# Revit family: Casement_30.5_E_Side_Hung_Standard
name_source: partatom
category: Windows
revit_build: Autodesk Revit 2014 (Build: 20130308_1515(x64)
units: mm (PartAtom-declared; Revit-internal decimal feet)

## types (17) — shared parameters
Aluminium Thickness = 1 mm  [stored 0.00328084 ft]
Area Pane Left Top = 0.52 m²
Bead SG Gap = 13 mm  [stored 0.0426509 ft]
Casement Dimension = 31 mm  [stored 0.101706 ft]
Custom Sash Height = 1154 mm  [stored 3.78609 ft]
Custom Sash Width = 554 mm  [stored 1.81759 ft]
DG Extrusion Start = 5 mm  [stored 0.0164042 ft]
DG Gasket Finish = Double Glazing Gasket Material
DG Thickness = 3 mm  [stored 0.00984252 ft]
Default Sill Height = 800 mm  [stored 2.62467 ft]
Depth Bead = 17 mm
Description = Window 30.5mm, Type E side hung
Double Glazing = No
Frame Center Offset = 15 mm  [stored 0.0492126 ft]
Height Panel 1 = 1139 mm  [stored 3.73688 ft]
Height Sash = 1124 mm  [stored 3.68766 ft]
Height Sash Opening = 1154 mm  [stored 3.78609 ft]
Length Transom = 540 mm  [stored 1.77165 ft]
Limit Fixed Pane Height Max = 1800 mm
Limit Fixed Pane Height Min = 200 mm  [stored 0.656168 ft]
Limit Fixed Pane Width Max = 1500 mm
Limit Fixed Pane Width Min = 200 mm  [stored 0.656168 ft]
Limit Sash Height Max = 1200 mm
Limit Sash Height Min = 300 mm  [stored 0.984252 ft]
Limit Sash Width Max = 600 mm  [stored 1.9685 ft]
Limit Sash Width Min = 300 mm  [stored 0.984252 ft]
Limit Window Height Max = 1860 mm
Limit Window Height Min = 1430 mm  [stored 4.6916 ft]
Limit Window Width Max = 2130 mm
Limit Window Width Min = 830 mm  [stored 2.7231 ft]
Manufacturer = Crealco
Max System DG One Piece Thickness = 3 mm  [stored 0.00984252 ft]
Max System DG Unit Thickness = 18 mm  [stored 0.0590551 ft]
Model = Casement 30.5
Offset Bead SG Center Reversed = 15 mm  [stored 0.0492126 ft]
Offset Mullion Left = 570 mm  [stored 1.87008 ft]
Offset Panel 3 Bead Top = 1200 mm
Offset Panel 4 Left = 600 mm  [stored 1.9685 ft]
Offset Sash Left = 23 mm  [stored 0.0754593 ft]
Offset Sash Top = 23 mm  [stored 0.0754593 ft]
Offset Transom Top = 1170 mm
Offset Window Exterior = 15 mm  [stored 0.0492126 ft]
SG Gasket Thickness = 6 mm  [stored 0.019685 ft]
Sash Center Offset = 12 mm  [stored 0.0393701 ft]
Sash Overlap = 7 mm  [stored 0.0229659 ft]
Sash Spacing Inner = 8 mm  [stored 0.0262467 ft]
URL = http://www.crealco.co.za
Wall Closure = By host
Width Bead = 15 mm  [stored 0.0492126 ft]
Width Fixed Pane Bottom LHS = 540 mm  [stored 1.77165 ft]
Width Panel 1 = 540 mm  [stored 1.77165 ft]
Width Profile = 30 mm  [stored 0.0984252 ft]
Width Sash = 524 mm  [stored 1.71916 ft]
Width Sash Opening = 554 mm  [stored 1.81759 ft]
zero-valued in all types: Window Exterior Offset

## per-type parameters (varying)
| type | Area Pane Left Bottom | Area Pane Right | Clearvue SHGC Value | Clearvue U Value | Custom Windload | Custom Window Height | Custom Window Width | DG Thickness Calc | Depth Mullion | Energy Advantage SHGC Value | Energy Advantage U Value | Height | Height Fixed Pane Bottom LHS | Height Fixed Pane RHS | Intruderprufe LowE SHGC Value | Intruderprufe LowE U Value | Intruderprufe SHGC Value | Intruderprufe U Value | Length Mullion | Max Pane Area | Mullion Depth Windload Based | Width | Width Fixed Pane RHS | Windload Design |
| 305-0915S-1000Pa | 0.13 m² | 0.36 m² | 0.627 | 6.69 | 1000 mm  [stored 3.28084 ft] | 1490 mm  [stored 4.88845 ft] | 890 mm  [stored 2.91995 ft] | 3 mm  [stored 0.00984252 ft] | 54 mm  [stored 0.177165 ft] | 0.563 | 5.23 | 1490 mm  [stored 4.88845 ft] | 260 mm  [stored 0.853018 ft] | 1430 mm  [stored 4.6916 ft] | 0.532 | 5.11 | 0.598 | 6.53 | 1490 mm  [stored 4.88845 ft] | 0.52 m² | 54 mm  [stored 0.177165 ft] | 890 mm  [stored 2.91995 ft] | 260 mm  [stored 0.853018 ft] | 1000 mm  [stored 3.28084 ft] |
| 305-1215S-1000Pa | 0.13 m² | 0.78 m² | 0.71 | 6.85 | 1000 mm  [stored 3.28084 ft] | 1490 mm  [stored 4.88845 ft] | 1190 mm  [stored 3.9042 ft] | 3 mm  [stored 0.00984252 ft] | 54 mm  [stored 0.177165 ft] | 0.635 | 5.15 | 1490 mm  [stored 4.88845 ft] | 260 mm  [stored 0.853018 ft] | 1430 mm  [stored 4.6916 ft] | 0.599 | 5.04 | 0.675 | 6.69 | 1490 mm  [stored 4.88845 ft] | 0.78 m² | 54 mm  [stored 0.177165 ft] | 1190 mm  [stored 3.9042 ft] | 560 mm | 1000 mm  [stored 3.28084 ft] |
| 305-1215S-2000Pa | 0.13 m² | 0.78 m² | 0.711 | 6.19 | 2000 mm | 1490 mm  [stored 4.88845 ft] | 1190 mm  [stored 3.9042 ft] | 3 mm  [stored 0.00984252 ft] | 70 mm  [stored 0.229659 ft] | 0.637 | 5.24 | 1490 mm  [stored 4.88845 ft] | 260 mm  [stored 0.853018 ft] | 1430 mm  [stored 4.6916 ft] | 0.6 | 5.12 | 0.677 | 6.76 | 1490 mm  [stored 4.88845 ft] | 0.78 m² | 70 mm  [stored 0.229659 ft] | 1190 mm  [stored 3.9042 ft] | 560 mm | 2000 mm |
| 305-1515S-1000Pa | 0.13 m² | 1.21 m² | 0.762 | 6.69 | 1000 mm  [stored 3.28084 ft] | 1490 mm  [stored 4.88845 ft] | 1490 mm  [stored 4.88845 ft] | 4 mm  [stored 0.0131234 ft] | 54 mm  [stored 0.177165 ft] | 0.682 | 5.11 | 1490 mm  [stored 4.88845 ft] | 260 mm  [stored 0.853018 ft] | 1430 mm  [stored 4.6916 ft] | 0.641 | 4.99 | 0.725 | 6.79 | 1490 mm  [stored 4.88845 ft] | 1.21 m² | 54 mm  [stored 0.177165 ft] | 1490 mm  [stored 4.88845 ft] | 860 mm  [stored 2.82152 ft] | 1000 mm  [stored 3.28084 ft] |
| 305-1515S-2000Pa | 0.13 m² | 1.21 m² | 0.763 | 7 | 2000 mm | 1490 mm  [stored 4.88845 ft] | 1490 mm  [stored 4.88845 ft] | 4 mm  [stored 0.0131234 ft] | 70 mm  [stored 0.229659 ft] | 0.683 | 5.17 | 1490 mm  [stored 4.88845 ft] | 260 mm  [stored 0.853018 ft] | 1430 mm  [stored 4.6916 ft] | 0.642 | 5.06 | 0.726 | 6.85 | 1490 mm  [stored 4.88845 ft] | 1.21 m² | 70 mm  [stored 0.229659 ft] | 1490 mm  [stored 4.88845 ft] | 860 mm  [stored 2.82152 ft] | 2000 mm |
| 305-0918S-1000Pa | 0.29 m² | 0.43 m² | 0.675 | 7 | 1000 mm  [stored 3.28084 ft] | 1790 mm | 890 mm  [stored 2.91995 ft] | 3 mm  [stored 0.00984252 ft] | 54 mm  [stored 0.177165 ft] | 0.605 | 5.45 | 1790 mm | 560 mm | 1730 mm | 0.572 | 5.29 | 0.644 | 6.84 | 1790 mm | 0.52 m² | 54 mm  [stored 0.177165 ft] | 890 mm  [stored 2.91995 ft] | 260 mm  [stored 0.853018 ft] | 1000 mm  [stored 3.28084 ft] |
| 305-0918S-1500Pa | 0.29 m² | 0.43 m² | 0.677 | 7.08 | 1500 mm | 1790 mm | 890 mm  [stored 2.91995 ft] | 3 mm  [stored 0.00984252 ft] | 70 mm  [stored 0.229659 ft] | 0.607 | 5.52 | 1790 mm | 560 mm | 1730 mm | 0.575 | 5.4 | 0.646 | 6.92 | 1790 mm | 0.52 m² | 70 mm  [stored 0.229659 ft] | 890 mm  [stored 2.91995 ft] | 260 mm  [stored 0.853018 ft] | 1500 mm |
| 305-1218S-1000Pa | 0.29 m² | 0.95 m² | 0.783 | 7.38 | 1000 mm  [stored 3.28084 ft] | 1790 mm | 1190 mm  [stored 3.9042 ft] | 3 mm  [stored 0.00984252 ft] | 54 mm  [stored 0.177165 ft] | 0.701 | 5.5 | 1790 mm | 560 mm | 1730 mm | 0.66 | 5.37 | 0.745 | 7.21 | 1790 mm | 0.95 m² | 54 mm  [stored 0.177165 ft] | 1190 mm  [stored 3.9042 ft] | 560 mm | 1000 mm  [stored 3.28084 ft] |
| 305-1218S-1500Pa | 0.29 m² | 0.95 m² | 0.784 | 7.45 | 1500 mm | 1790 mm | 1190 mm  [stored 3.9042 ft] | 3 mm  [stored 0.00984252 ft] | 70 mm  [stored 0.229659 ft] | 0.702 | 5.58 | 1790 mm | 560 mm | 1730 mm | 0.662 | 5.46 | 0.747 | 7.28 | 1790 mm | 0.95 m² | 70 mm  [stored 0.229659 ft] | 1190 mm  [stored 3.9042 ft] | 560 mm | 1500 mm |
| 305-1518S-1000Pa | 0.29 m² | 1.46 m² | 0 | 7.9 | 1000 mm  [stored 3.28084 ft] | 1790 mm | 1490 mm  [stored 4.88845 ft] | 4 mm  [stored 0.0131234 ft] | 70 mm  [stored 0.229659 ft] | 0 | 7.9 | 1790 mm | 560 mm | 1730 mm | 0.719 | 5.5 | 0.814 | 7.51 | 1790 mm | 1.46 m² | 70 mm  [stored 0.229659 ft] | 1490 mm  [stored 4.88845 ft] | 860 mm  [stored 2.82152 ft] | 1000 mm  [stored 3.28084 ft] |
| 305-0915S-1500Pa | 0.13 m² | 0.36 m² | 0.627 | 6.69 | 1500 mm | 1490 mm  [stored 4.88845 ft] | 890 mm  [stored 2.91995 ft] | 3 mm  [stored 0.00984252 ft] | 54 mm  [stored 0.177165 ft] | 0.563 | 5.23 | 1490 mm  [stored 4.88845 ft] | 260 mm  [stored 0.853018 ft] | 1430 mm  [stored 4.6916 ft] | 0.532 | 5.11 | 0.598 | 6.53 | 1490 mm  [stored 4.88845 ft] | 0.52 m² | 54 mm  [stored 0.177165 ft] | 890 mm  [stored 2.91995 ft] | 260 mm  [stored 0.853018 ft] | 1500 mm |
| 305-0915S-2000Pa | 0.13 m² | 0.36 m² | 0.627 | 6.69 | 2000 mm | 1490 mm  [stored 4.88845 ft] | 890 mm  [stored 2.91995 ft] | 3 mm  [stored 0.00984252 ft] | 54 mm  [stored 0.177165 ft] | 0.563 | 5.23 | 1490 mm  [stored 4.88845 ft] | 260 mm  [stored 0.853018 ft] | 1430 mm  [stored 4.6916 ft] | 0.532 | 5.11 | 0.598 | 6.53 | 1490 mm  [stored 4.88845 ft] | 0.52 m² | 54 mm  [stored 0.177165 ft] | 890 mm  [stored 2.91995 ft] | 260 mm  [stored 0.853018 ft] | 2000 mm |
| 305-0918S-2000Pa | 0.29 m² | 0.43 m² | 0.677 | 7.08 | 2000 mm | 1790 mm | 890 mm  [stored 2.91995 ft] | 3 mm  [stored 0.00984252 ft] | 70 mm  [stored 0.229659 ft] | 0.607 | 5.52 | 1790 mm | 560 mm | 1730 mm | 0.575 | 5.4 | 0.646 | 6.92 | 1790 mm | 0.52 m² | 70 mm  [stored 0.229659 ft] | 890 mm  [stored 2.91995 ft] | 260 mm  [stored 0.853018 ft] | 2000 mm |
| 305-1215S-1500Pa | 0.13 m² | 0.78 m² | 0.71 | 6.85 | 1500 mm | 1490 mm  [stored 4.88845 ft] | 1190 mm  [stored 3.9042 ft] | 3 mm  [stored 0.00984252 ft] | 54 mm  [stored 0.177165 ft] | 0.635 | 5.15 | 1490 mm  [stored 4.88845 ft] | 260 mm  [stored 0.853018 ft] | 1430 mm  [stored 4.6916 ft] | 0.599 | 5.04 | 0.675 | 6.69 | 1490 mm  [stored 4.88845 ft] | 0.78 m² | 54 mm  [stored 0.177165 ft] | 1190 mm  [stored 3.9042 ft] | 560 mm | 1500 mm |
| 305-1218S-2000Pa | 0.29 m² | 0.95 m² | 0.784 | 7.45 | 2000 mm | 1790 mm | 1190 mm  [stored 3.9042 ft] | 3 mm  [stored 0.00984252 ft] | 70 mm  [stored 0.229659 ft] | 0.702 | 5.58 | 1790 mm | 560 mm | 1730 mm | 0.662 | 5.46 | 0.747 | 7.28 | 1790 mm | 0.95 m² | 70 mm  [stored 0.229659 ft] | 1190 mm  [stored 3.9042 ft] | 560 mm | 2000 mm |
| 305-1515S-1500Pa | 0.13 m² | 1.21 m² | 0.762 | 6.69 | 1500 mm | 1490 mm  [stored 4.88845 ft] | 1490 mm  [stored 4.88845 ft] | 4 mm  [stored 0.0131234 ft] | 54 mm  [stored 0.177165 ft] | 0.682 | 5.11 | 1490 mm  [stored 4.88845 ft] | 260 mm  [stored 0.853018 ft] | 1430 mm  [stored 4.6916 ft] | 0.641 | 4.99 | 0.725 | 6.79 | 1490 mm  [stored 4.88845 ft] | 1.21 m² | 54 mm  [stored 0.177165 ft] | 1490 mm  [stored 4.88845 ft] | 860 mm  [stored 2.82152 ft] | 1500 mm |
| 305-1518S-1500Pa | 0.29 m² | 1.46 m² | 0 | 7.9 | 1500 mm | 1790 mm | 1490 mm  [stored 4.88845 ft] | 4 mm  [stored 0.0131234 ft] | 70 mm  [stored 0.229659 ft] | 0 | 7.9 | 1790 mm | 560 mm | 1730 mm | 0.719 | 5.5 | 0.814 | 7.51 | 1790 mm | 1.46 m² | 70 mm  [stored 0.229659 ft] | 1490 mm  [stored 4.88845 ft] | 860 mm  [stored 2.82152 ft] | 1500 mm |

note: [stored X ft] marks values corroborated as IEEE doubles in the binary element streams (Revit-internal decimal feet)

## geometry (parser evidence)
native form markers: Blend x4, Extrusion x1, Sweep x28
no freeform markers — native parametric forms only
